# Revit family: Grab_Bar-90_Degree-Bobrick-B-5854_Series
name_source: partatom
category: Specialty Equipment
units: mm (PartAtom-declared; Revit-internal decimal feet)

## family parameters
Cut with Voids When Loaded = No
Host = Face
OmniClass Number = 23.40.20.21.47
OmniClass Title = Bath Grab Bars
Part Type = Normal
Room Calculation Point = No
Round Connector Dimension = Use Diameter
Shared = Yes

## types (2) — shared parameters
251-4 WingIt Grab Bar Fastener = No
252-30 Mounting Kit = No
2583 Anchor Device = No
2586 Anchor Device = No
ADA Compliant = Yes
Assembly Code = C1030200
Concealed Mounting Flanges Material = Metal-Bobrick-Stainless Steel
Default Elevation = 30"
Description = 11/4" (32mm) DIAMETER STAINLESS STEEL 40" x 30" (1016 x 762mm)
90-DEGREE GRAB BAR - PEENED FINISH
Grab Bar Diameter = 1 1/4"
Grab Bar Material = Stainless Steel-Bobrick-Satin
Height = 30"
Installation Type = Wall Mounted
Manufacturer = Bobrick
Material = Stainless Steel-Bobrick-Satin
Price = Prices may vary. Please consult Manufacturer Representative for most up-to-date price list.
Snap Flange Cover Depth = 5/8"
Snap Flange Cover Diameter = 3 1/4"
Snap Flange Covers Material = Stainless Steel-Bobrick-Satin
Support Load = 900 pounds (408kg)
URL = http://www.bobrick.com
Wall Clearance From Grab Bar = 1 1/2"
Warranty Documentation Link = https://www.bobrick.com
Width = 40"

## per-type parameters (varying)
| type | B-5854.99 | Type Comments |
| B-5854.99 | Yes | 40" to the left |
| B-58546.99 | No | 40" to the right |

note: column(s) folded — value = type name in every type: Model

type visibility flags (boolean, named after types; folded from table):
- B-5854.99: Yes: (none)
- B-58546.99: Yes: B-58546.99

## geometry (parser evidence)
native form markers: Sweep x4
no freeform markers — native parametric forms only
